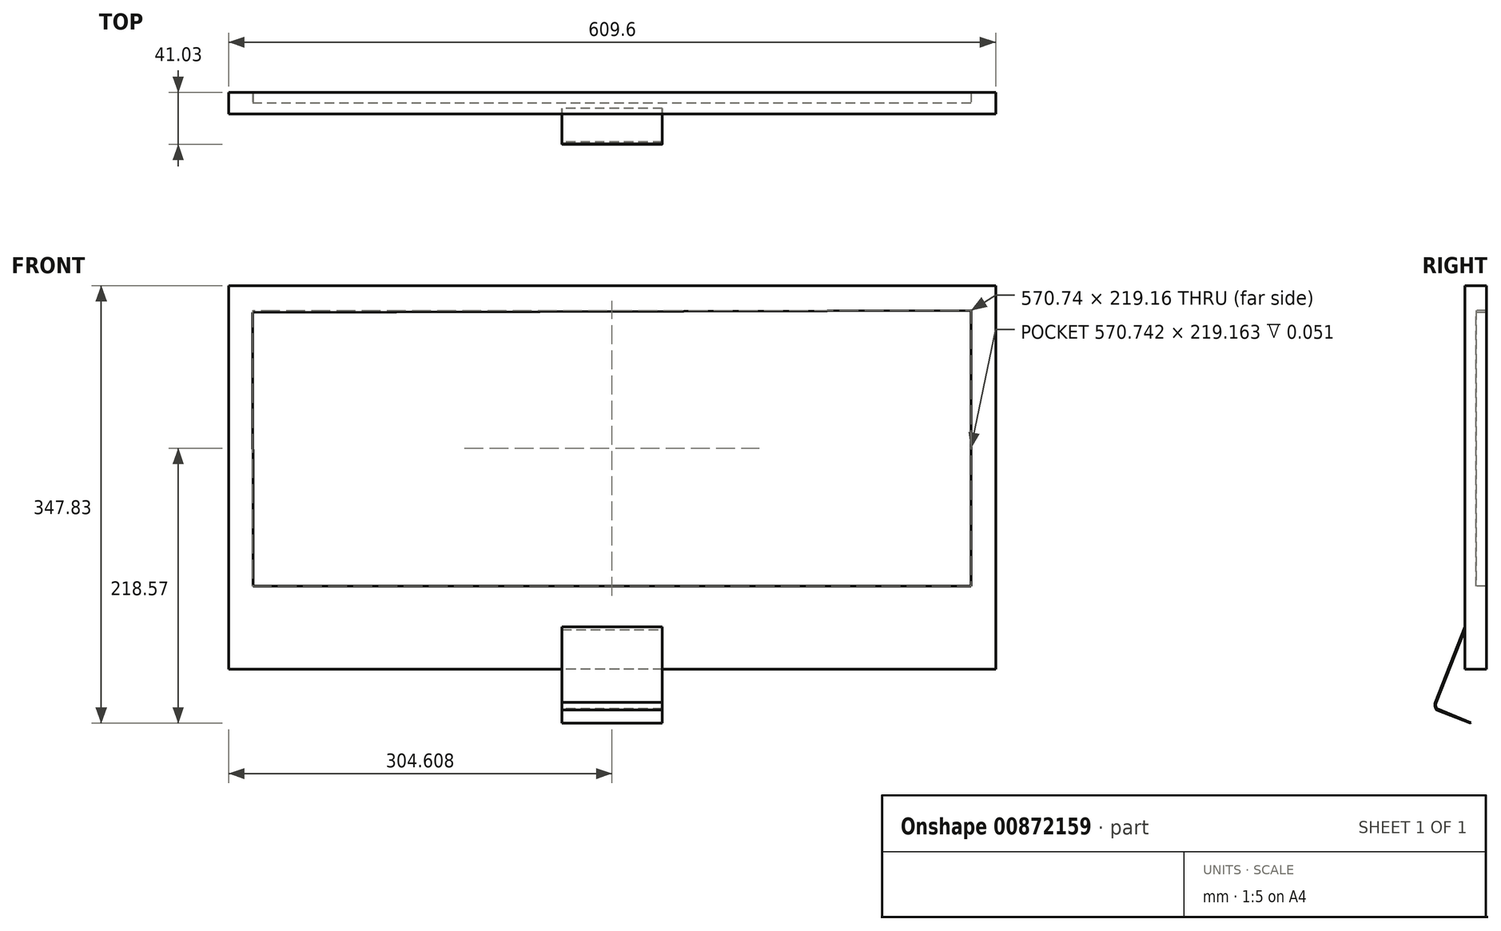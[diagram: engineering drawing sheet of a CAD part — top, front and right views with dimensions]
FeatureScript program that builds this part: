
annotation { "Feature Type Name" : "Feature", "Feature Type Description" : "" }
export const myFeature = defineFeature(function(context is Context, id is Id, definition is map)
    precondition{}
    {
        {
            var Q0;
            Q0=qCreatedBy(makeId("Front.planeOp"),FACE);
            var sketch = newSketch(context, id + "F0", { "sketchPlane" : qUnion([Q0])});
            skLineSegment(sketch, "E0.bottom", {"start": v(304.8, 152.4) * mm, "end": v(-304.8, 152.4) * mm});
            skLineSegment(sketch, "E0.top", {"start": v(304.8, -152.4) * mm, "end": v(-304.8, -152.4) * mm});
            skLineSegment(sketch, "E0.left", {"start": v(304.8, 152.4) * mm, "end": v(304.8, -152.4) * mm});
            skLineSegment(sketch, "E0.right", {"start": v(-304.8, 152.4) * mm, "end": v(-304.8, -152.4) * mm});
            skPoint(sketch, "E0.middle", {"position": v(0, 0) * mm});
            skLineSegment(sketch, "E1.bottom", {"start": v(285.18, -86.44) * mm, "end": v(-285.18, -86.44) * mm});
            skPoint(sketch, "E1.top.start.orphan", {"position": v(285.18, 86.44) * mm});
            skPoint(sketch, "E1.right.end.orphan", {"position": v(-285.18, 86.44) * mm});
            skLineSegment(sketch, "E2", {"start": v(285.18, 132.72) * mm, "end": v(285.18, -86.44) * mm});
            skLineSegment(sketch, "E3", {"start": v(285.18, 132.72) * mm, "end": v(-285.56, 131.14) * mm});
            skLineSegment(sketch, "E4", {"start": v(-285.18, -86.44) * mm, "end": v(-285.56, 131.14) * mm});
            skSolve(sketch);
        }
        {
            var Q0;
            Q0=makeQuery(id+"F0.imprint","IMPRINT",FACE,{"disambiguationData":[TD([[makeQuery(id+"F0.imprint","IMPRINT",EDGE,{"derivedFrom":sQuery(id+"F0.wireOp",EDGE,"E1.bottom")}),-1.0]])]});
            extrude(context, id + "F1", {"entities" : qUnion([Q0]), "endBound" : BoundingType.SYMMETRIC, "depth" : 8.64 * mm, "offsetDistance" : 25.4 * mm});
        }
        {
            var Q0;
            Q0=makeQuery(id+"F0.imprint","IMPRINT",FACE,{"disambiguationData":[TD([[makeQuery(id+"F0.imprint","IMPRINT",EDGE,{"derivedFrom":sQuery(id+"F0.wireOp",EDGE,"E0.bottom")}),1.0]])]});
            extrude(context, id + "F2", {"entities" : qUnion([Q0]), "operationType" : NewBodyOperationType.ADD, "endBound" : BoundingType.SYMMETRIC, "depth" : 25.4 * mm, "offsetDistance" : 25.4 * mm});
        }
        {
            var Q0;
            Q0=makeQuery(id+"F2.opExtrude","CAP_FACE",FACE,{"disambiguationData":[OSD([sQuery(id+"F0.wireOp",EDGE,"E0.bottom"),sQuery(id+"F0.wireOp",EDGE,"E0.top"),sQuery(id+"F0.wireOp",EDGE,"E0.left"),sQuery(id+"F0.wireOp",EDGE,"E0.right"),sQuery(id+"F0.wireOp",EDGE,"E1.bottom"),sQuery(id+"F0.wireOp",EDGE,"E1.top"),sQuery(id+"F0.wireOp",EDGE,"E1.left"),sQuery(id+"F0.wireOp",EDGE,"E1.right")])],"isStart":false});
            extrude(context, id + "F3", {"entities" : qUnion([Q0]), "operationType" : NewBodyOperationType.REMOVE, "oppositeDirection" : true, "depth" : 8.33 * mm, "offsetDistance" : 25.4 * mm});
        }
        {
            var Q0;
            Q0=makeQuery(id+"F1.opExtrude","CAP_FACE",FACE,{"disambiguationData":[OSD([sQuery(id+"F0.wireOp",EDGE,"E1.bottom"),sQuery(id+"F0.wireOp",EDGE,"E2"),sQuery(id+"F0.wireOp",EDGE,"E3"),sQuery(id+"F0.wireOp",EDGE,"E4")])],"isStart":true});
            extrude(context, id + "F4", {"entities" : qUnion([Q0]), "depth" : 8.38 * mm, "offsetDistance" : 25.4 * mm});
        }
        {
            var Q0;
            Q0=qCreatedBy(makeId("Right.planeOp"),FACE);
            var sketch = newSketch(context, id + "F5", { "sketchPlane" : qUnion([Q0])});
            skLineSegment(sketch, "E5", {"start": v(0, -107.52) * mm, "end": v(-28.03, -178.9) * mm});
            skLineSegment(sketch, "E6", {"start": v(-27.02, -184.82) * mm, "end": v(0, -195.43) * mm});
            skArc(sketch, "E7", {"start": v(-28.03, -178.9) * mm, "mid": v(-28.24, -181.98) * mm, "end": v(-27.02, -184.82) * mm});
            skLineSegment(sketch, "E8", {"start": v(0, -109.75) * mm, "end": v(-27.25, -179.15) * mm});
            skArc(sketch, "E9", {"start": v(-27.25, -179.15) * mm, "mid": v(-27.51, -181.69) * mm, "end": v(-26.43, -184) * mm});
            skLineSegment(sketch, "E10", {"start": v(0, -195.43) * mm, "end": v(0.17, -195) * mm});
            skLineSegment(sketch, "E11", {"start": v(0.17, -195) * mm, "end": v(-26.43, -184) * mm});
            skLineSegment(sketch, "E12", {"start": v(0, -107.52) * mm, "end": v(0, -109.75) * mm});
            skSolve(sketch);
        }
        {
            var Q0;
            Q0 = qSketchRegion(id + "F5", true);
            extrude(context, id + "F6", {"entities" : qUnion([Q0]), "operationType" : NewBodyOperationType.ADD, "endBound" : BoundingType.SYMMETRIC, "depth" : 79.76 * mm, "offsetDistance" : 25.4 * mm});
        }
    });
